# Revit family: Sanitary_Showers_AXOR_10625800-AXOR-ShowerCollection-ShowerHea
name_source: partatom
category: Plumbing Fixtures
revit_build: Autodesk Revit 2015 (Build: 20140606_1530(x64)
units: mm (PartAtom-declared; Revit-internal decimal feet)

## types (1)
- Stainless Steel
    BIMobject category = Showers
    BIMobject category code = sanitary-showers
    BIMobject main category = Sanitary
    BIMobject main category code = sanitary
    BOSUseNativeGeometries = 1
    Brand url = https://www.axor-design.com
    Default Elevation = 4' - 0"
    Design country = Germany
    EAN code = https://4011097585772
    Edition number = 1
    IFC Classification = Sanitary Terminal
    Installation instructions = https://pro.hansgrohe-int.com
    Manufacturer country = Germany
    Manufacturer name = AXOR
    Product Guid = ad1d6a23-b2f1-4a06-9f28-5360e5e3c326
    Product SKU = 10625800
    Product data url = https://bimobject.com
    Product family = AXOR ShowerCollection
    Product group = Overhead showers
    Product name = AXOR ShowerCollection ShowerHeaven 720 x 720 mm 3jet overhead shower 10625800
    Product url = https://pro.hansgrohe-int.com
    QR code = http://bimobject.com
    Technical description = https://pro.hansgrohe-int.com

## geometry (parser evidence)
native form markers: Sweep x2
no freeform markers — native parametric forms only
